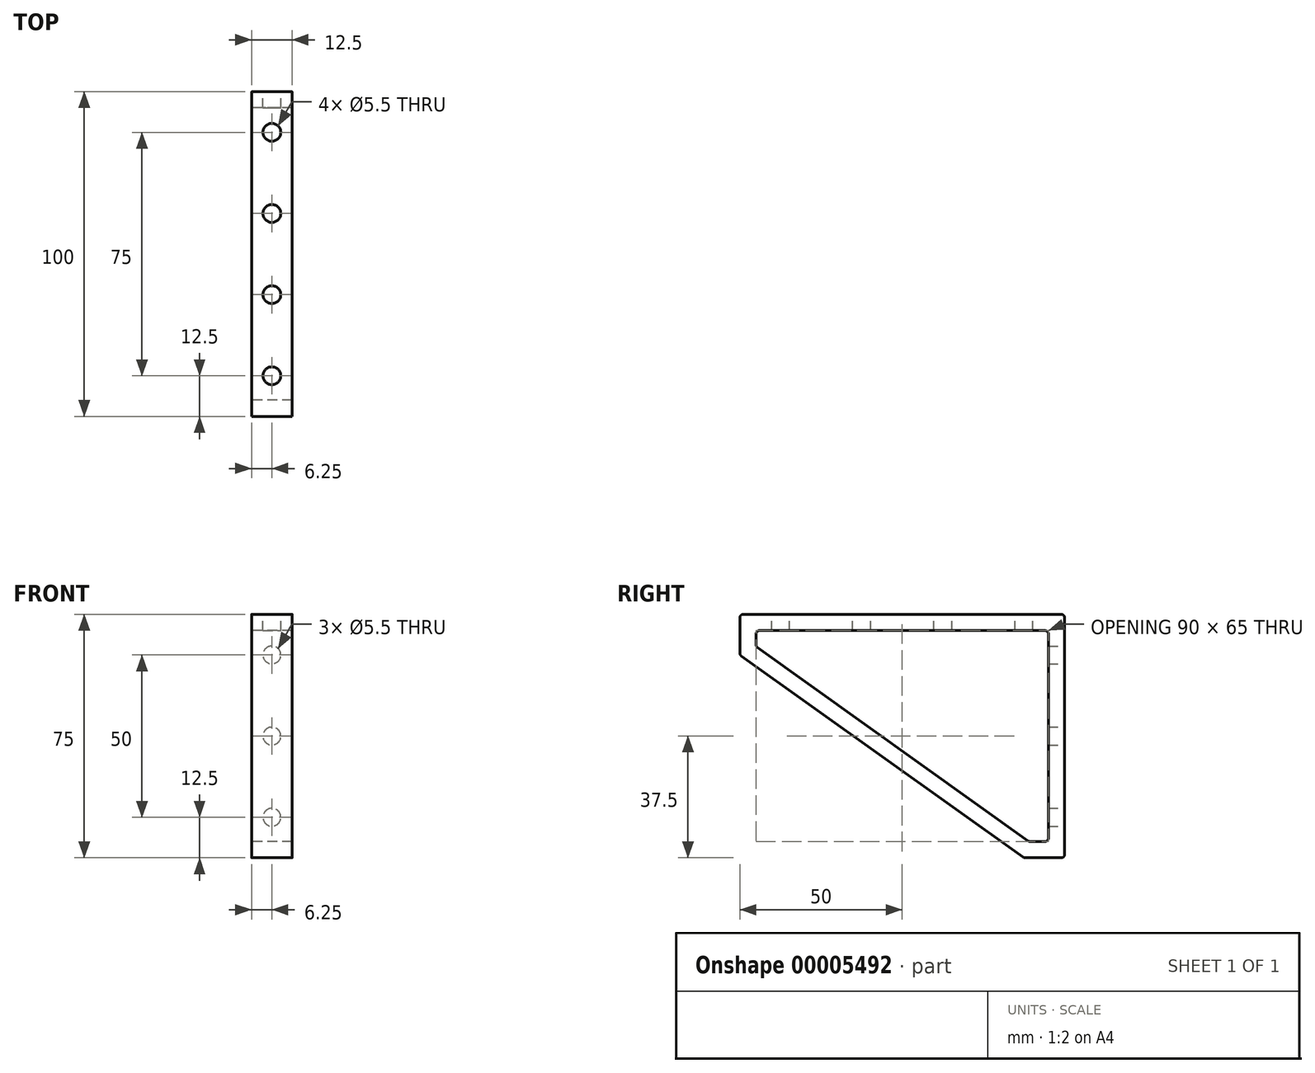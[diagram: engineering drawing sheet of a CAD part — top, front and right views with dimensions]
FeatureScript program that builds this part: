
annotation { "Feature Type Name" : "Feature", "Feature Type Description" : "" }
export const myFeature = defineFeature(function(context is Context, id is Id, definition is map)
    precondition{}
    {
        {
            var Q0;
            Q0=qCreatedBy(makeId("Right.planeOp"),FACE);
            var sketch = newSketch(context, id + "F0", { "sketchPlane" : qUnion([Q0])});
            skLineSegment(sketch, "E0", {"start": v(0, 0) * mm, "end": v(0, -75) * mm});
            skLineSegment(sketch, "E1", {"start": v(0, 0) * mm, "end": v(-100, 0) * mm});
            skLineSegment(sketch, "E2", {"start": v(-100, 0) * mm, "end": v(-100, -12.5) * mm});
            skLineSegment(sketch, "E3", {"start": v(-100, -12.5) * mm, "end": v(-12.5, -75) * mm});
            skLineSegment(sketch, "E4", {"start": v(0, -75) * mm, "end": v(-12.5, -75) * mm});
            skSolve(sketch);
        }
        {
            var Q0;
            Q0=makeQuery(id+"F0.imprint","IMPRINT",FACE,{"disambiguationData":[TD([[makeQuery(id+"F0.imprint","IMPRINT",EDGE,{"derivedFrom":sQuery(id+"F0.wireOp",EDGE,"E0")}),-1.0]])]});
            extrude(context, id + "F1", {"entities" : qUnion([Q0]), "depth" : 12.5 * mm});
        }
        {
            var Q0;
            Q0=makeQuery(id+"F1.opExtrude","CAP_FACE",FACE,{"disambiguationData":[OSD([sQuery(id+"F0.wireOp",EDGE,"E0"),sQuery(id+"F0.wireOp",EDGE,"E1"),sQuery(id+"F0.wireOp",EDGE,"33bea93b-b1e7-484a-a300-cced40a43aed")])],"isStart":true});
            var Q1;
            Q1=makeQuery(id+"F1.opExtrude","CAP_FACE",FACE,{"disambiguationData":[OSD([sQuery(id+"F0.wireOp",EDGE,"E0"),sQuery(id+"F0.wireOp",EDGE,"E1"),sQuery(id+"F0.wireOp",EDGE,"33bea93b-b1e7-484a-a300-cced40a43aed")])],"isStart":false});
            shell(context, id + "F2", {"entities" : qUnion([Q0, Q1]), "thickness" : 5 * mm});
        }
        {
            var Q0;
            Q0=makeQuery(id+"F1.opExtrude","SWEPT_FACE",FACE,{"disambiguationData":[OSD([sQuery(id+"F0.wireOp",EDGE,"E0")])]});
            var sketch = newSketch(context, id + "F3", { "sketchPlane" : qUnion([Q0])});
            skCircle(sketch, "E5", {"center": v(-6.25, -12.5) * mm, "radius": 2.75 * mm});
            skPoint(sketch, "E6", {"position": v(-6.25, 0) * mm});
            skCircle(sketch, "E7.0.1.0", {"center": v(-6.25, -37.5) * mm, "radius": 2.75 * mm});
            skCircle(sketch, "E7.0.2.0", {"center": v(-6.25, -62.5) * mm, "radius": 2.75 * mm});
            skCircle(sketch, "E7.0.3.0", {"center": v(-6.25, -87.5) * mm, "radius": 2.75 * mm});
            skCircle(sketch, "E7.0.4.0", {"center": v(-6.25, -112.5) * mm, "radius": 2.75 * mm});
            skLineSegment(sketch, "E7.direction1", {"start": v(-6.25, -12.5) * mm, "end": v(18.75, -12.5) * mm, "construction": true});
            skLineSegment(sketch, "E7.direction2", {"start": v(-6.25, -12.5) * mm, "end": v(-6.25, -37.5) * mm, "construction": true});
            skSolve(sketch);
        }
        {
            var Q0;
            Q0=qSketchRegion(id+"F3",true);
            var Q1;
            Q1=makeQuery(id+"F2.opShell","OFFSET_FACE",FACE,{"disambiguationData":[OSD([sQuery(id+"F0.wireOp",EDGE,"E0")])]});
            extrude(context, id + "F4", {"entities" : qUnion([Q0]), "operationType" : NewBodyOperationType.REMOVE, "endBound" : BoundingType.UP_TO_SURFACE, "oppositeDirection" : true, "endBoundEntityFace" : qUnion([Q1]), "depth" : 25 * mm});
        }
        {
            var Q0;
            Q0=makeQuery(id+"F1.opExtrude","SWEPT_FACE",FACE,{"disambiguationData":[OSD([sQuery(id+"F0.wireOp",EDGE,"E1")])]});
            var sketch = newSketch(context, id + "F5", { "sketchPlane" : qUnion([Q0])});
            skPoint(sketch, "E8", {"position": v(6.25, 0) * mm});
            skCircle(sketch, "E9", {"center": v(6.25, -12.5) * mm, "radius": 2.75 * mm});
            skCircle(sketch, "E10.0.1.0", {"center": v(6.25, -37.5) * mm, "radius": 2.75 * mm});
            skCircle(sketch, "E10.0.2.0", {"center": v(6.25, -62.5) * mm, "radius": 2.75 * mm});
            skLineSegment(sketch, "E10.direction1", {"start": v(6.25, -12.5) * mm, "end": v(35, -12.5) * mm, "construction": true});
            skLineSegment(sketch, "E10.direction2", {"start": v(6.25, -12.5) * mm, "end": v(6.25, -37.5) * mm, "construction": true});
            skCircle(sketch, "E11.0.0.3", {"center": v(6.25, -87.5) * mm, "radius": 2.75 * mm});
            skCircle(sketch, "E11.0.0.4", {"center": v(6.25, -112.5) * mm, "radius": 2.75 * mm});
            skSolve(sketch);
        }
        {
            var Q0;
            {Q0=qUnion([makeQuery(id+"F5.imprint","IMPRINT",FACE,{"disambiguationData":[TD([[makeQuery(id+"F5.imprint","IMPRINT",EDGE,{"derivedFrom":sQuery(id+"F5.wireOp",EDGE,"E11.0.0.4")}),1.0]])]}),makeQuery(id+"F5.imprint","IMPRINT",FACE,{"disambiguationData":[TD([[makeQuery(id+"F5.imprint","IMPRINT",EDGE,{"derivedFrom":sQuery(id+"F5.wireOp",EDGE,"E9")}),1.0]])]}),makeQuery(id+"F5.imprint","IMPRINT",FACE,{"disambiguationData":[TD([[makeQuery(id+"F5.imprint","IMPRINT",EDGE,{"derivedFrom":sQuery(id+"F5.wireOp",EDGE,"E10.0.1.0")}),1.0]])]}),makeQuery(id+"F5.imprint","IMPRINT",FACE,{"disambiguationData":[TD([[makeQuery(id+"F5.imprint","IMPRINT",EDGE,{"derivedFrom":sQuery(id+"F5.wireOp",EDGE,"E10.0.2.0")}),1.0]])]}),makeQuery(id+"F5.imprint","IMPRINT",FACE,{"disambiguationData":[TD([[makeQuery(id+"F5.imprint","IMPRINT",EDGE,{"derivedFrom":sQuery(id+"F5.wireOp",EDGE,"E11.0.0.3")}),1.0]])]})]);}
            var Q1;
            Q1=makeQuery(id+"F2.opShell","OFFSET_FACE",FACE,{"disambiguationData":[OSD([sQuery(id+"F0.wireOp",EDGE,"E1")])]});
            extrude(context, id + "F6", {"entities" : qUnion([Q0]), "operationType" : NewBodyOperationType.REMOVE, "endBound" : BoundingType.UP_TO_SURFACE, "oppositeDirection" : true, "endBoundEntityFace" : qUnion([Q1]), "depth" : 25 * mm});
        }
        {
            var Q0;
            Q0=makeQuery(id+"F2.opShell","OFFSET_EDGE",EDGE,{"disambiguationData":[OSD([sQuery(id+"F0.wireOp",EDGE,"E0"),sQuery(id+"F0.wireOp",EDGE,"E1")])]});
            var Q1;
            Q1=makeQuery(id+"F2.opShell","OFFSET_EDGE",EDGE,{"disambiguationData":[OSD([sQuery(id+"F0.wireOp",EDGE,"E1"),sQuery(id+"F0.wireOp",EDGE,"E2")])]});
            var Q2;
            Q2=makeQuery(id+"F2.opShell","OFFSET_EDGE",EDGE,{"disambiguationData":[OSD([sQuery(id+"F0.wireOp",EDGE,"E2"),sQuery(id+"F0.wireOp",EDGE,"E3")])]});
            var Q3;
            Q3=makeQuery(id+"F2.opShell","OFFSET_EDGE",EDGE,{"disambiguationData":[OSD([sQuery(id+"F0.wireOp",EDGE,"E3"),sQuery(id+"F0.wireOp",EDGE,"E4")])]});
            var Q4;
            Q4=makeQuery(id+"F2.opShell","OFFSET_EDGE",EDGE,{"disambiguationData":[OSD([sQuery(id+"F0.wireOp",EDGE,"E0"),sQuery(id+"F0.wireOp",EDGE,"E4")])]});
            var Q5;
            Q5=makeQuery(id+"F1.opExtrude","SWEPT_EDGE",EDGE,{"disambiguationData":[OSD([sQuery(id+"F0.wireOp",EDGE,"E0"),sQuery(id+"F0.wireOp",EDGE,"E4")])]});
            var Q6;
            Q6=makeQuery(id+"F1.opExtrude","SWEPT_EDGE",EDGE,{"disambiguationData":[OSD([sQuery(id+"F0.wireOp",EDGE,"E3"),sQuery(id+"F0.wireOp",EDGE,"E4")])]});
            var Q7;
            Q7=makeQuery(id+"F1.opExtrude","SWEPT_EDGE",EDGE,{"disambiguationData":[OSD([sQuery(id+"F0.wireOp",EDGE,"E2"),sQuery(id+"F0.wireOp",EDGE,"E3")])]});
            var Q8;
            Q8=makeQuery(id+"F1.opExtrude","SWEPT_EDGE",EDGE,{"disambiguationData":[OSD([sQuery(id+"F0.wireOp",EDGE,"E0"),sQuery(id+"F0.wireOp",EDGE,"E1")])]});
            var Q9;
            Q9=makeQuery(id+"F1.opExtrude","SWEPT_EDGE",EDGE,{"disambiguationData":[OSD([sQuery(id+"F0.wireOp",EDGE,"E1"),sQuery(id+"F0.wireOp",EDGE,"E2")])]});
            fillet(context, id + "F7", {"entities" : qUnion([Q0, Q1, Q2, Q3, Q4, Q5, Q6, Q7, Q8, Q9]), "radius" : 1 * mm, "tangentPropagation" : true, "allowEdgeOverflow" : false});
        }
    });
